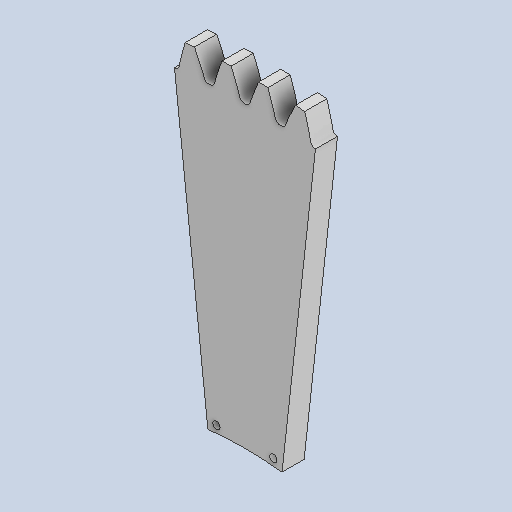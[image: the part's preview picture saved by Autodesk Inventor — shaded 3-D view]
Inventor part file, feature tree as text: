
AUTODESK INVENTOR PART (.ipt)
format: ipt  version: 2025 (Build 290162010, 162A)  size: 658,944 bytes
history: native  units: mm
features: extrude x3, sketch x2, pattern_circular x1, hole x1, projected_geometry x1
ambient origin geometry x8: Origin, YZ Plane, XZ Plane, XY Plane, X Axis, Y Axis, Z Axis, Center Point
bodies: Body1 (feature_tree)
feature tree (8):
  extrude  "Extrusion1"  Depth=27.0mm TaperAngle=0.0deg
  extrude  "Extrusion2"  Depth=4.0mm
  pattern_circular  "Circular Pattern1"  [2 undecoded]
  extrude  "Extrusion3"  TaperAngle=0.0deg  [1 undecoded]
  hole  "Hole1"  [1 undecoded]
  sketch  "Sketch2"  dims[d0=24.0mm d1=0.0mm d2=27.0mm d3=0.0mm]
  projected_geometry  "Projected Loop1"
  sketch  "Sketch3"  dims[d4=1120.0mm d5=360.0deg d7=720.0mm d8=2.243998mm d9=0.0mm d10=0.0mm d11=735.0mm d12=1.68337mm d13=8.0mm d14=6.0mm d15=4.0mm d16=2.0mm d17=90.0deg d18=8.0mm d19=20.594885mm]
note: 4 required parameter values undecoded (feature->parameter linkage not recoverable at this tier; creation-order binding heuristic only, values carry confidence <= 0.55)
